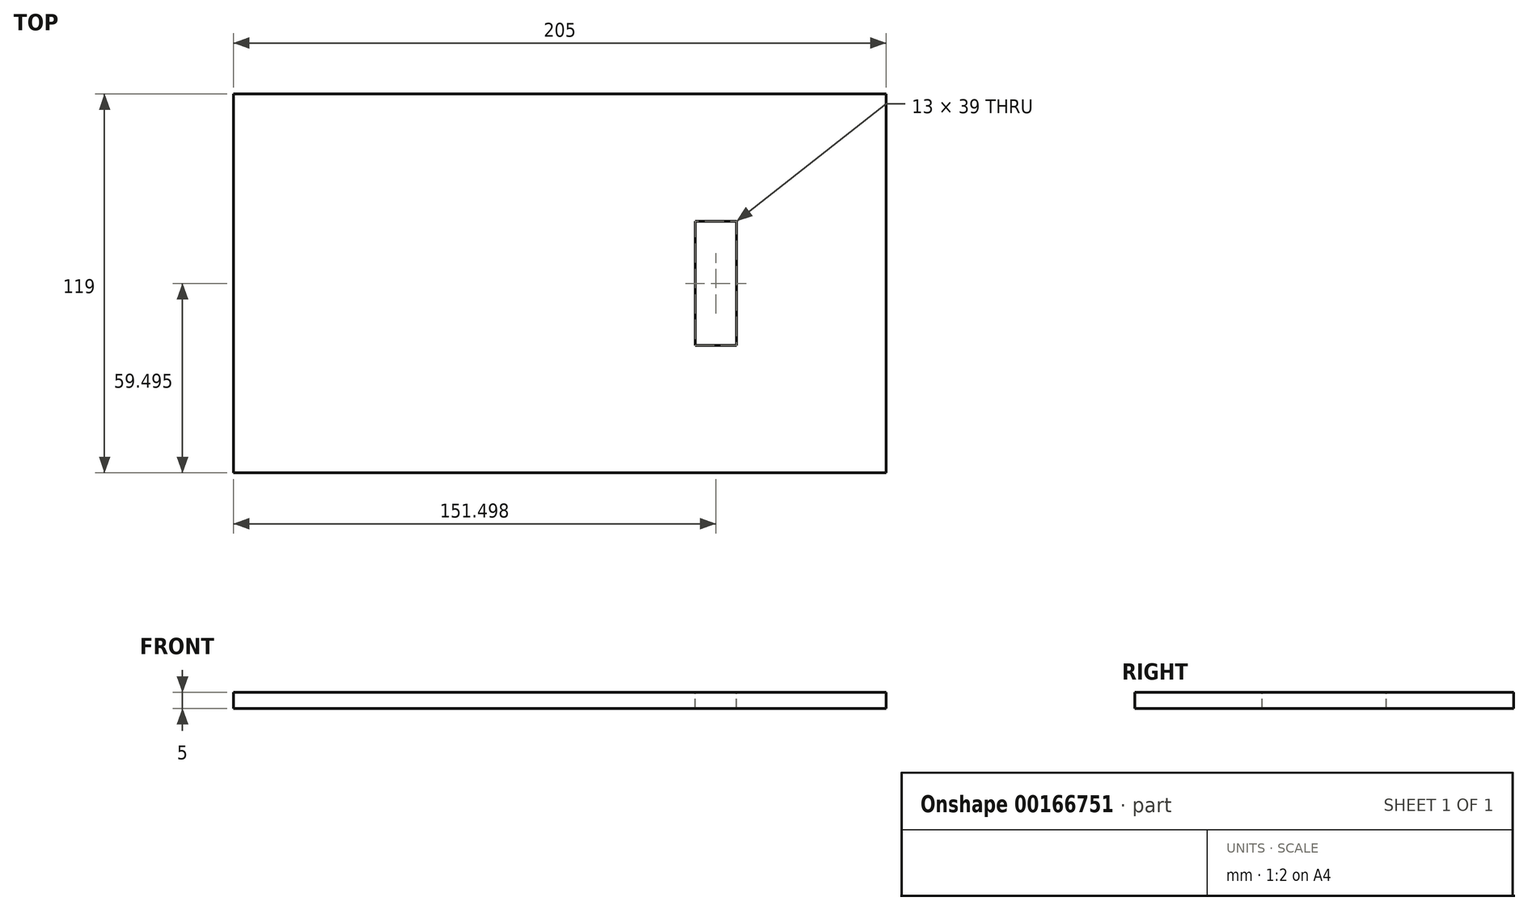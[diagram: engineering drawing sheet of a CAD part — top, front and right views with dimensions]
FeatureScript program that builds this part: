
annotation { "Feature Type Name" : "Feature", "Feature Type Description" : "" }
export const myFeature = defineFeature(function(context is Context, id is Id, definition is map)
    precondition{}
    {
        {
            var Q0;
            Q0=qCreatedBy(makeId("Top.planeOp"),FACE);
            var sketch = newSketch(context, id + "F0", { "sketchPlane" : qUnion([Q0])});
            skLineSegment(sketch, "E0.bottom", {"start": v(-194.6, 79.63) * mm, "end": v(10.4, 79.63) * mm});
            skLineSegment(sketch, "E0.top", {"start": v(-194.6, -39.37) * mm, "end": v(10.4, -39.37) * mm});
            skLineSegment(sketch, "E0.left", {"start": v(-194.6, 79.63) * mm, "end": v(-194.6, -39.37) * mm});
            skLineSegment(sketch, "E0.right", {"start": v(10.4, 79.63) * mm, "end": v(10.4, -39.37) * mm});
            skSolve(sketch);
        }
        {
            var Q0;
            Q0 = qSketchRegion(id + "F0", true);
            extrude(context, id + "F1", {"entities" : qUnion([Q0]), "depth" : 5 * mm, "offsetDistance" : 25 * mm});
        }
        {
            var Q0;
            Q0=makeQuery(id+"F1.opExtrude","CAP_FACE",FACE,{"disambiguationData":[OSD([sQuery(id+"F0.wireOp",EDGE,"E0.bottom"),sQuery(id+"F0.wireOp",EDGE,"E0.top"),sQuery(id+"F0.wireOp",EDGE,"E0.left"),sQuery(id+"F0.wireOp",EDGE,"E0.right")])],"isStart":false});
            var sketch = newSketch(context, id + "F2", { "sketchPlane" : qUnion([Q0])});
            skLineSegment(sketch, "E1.bottom", {"start": v(-49.6, 39.63) * mm, "end": v(-36.6, 39.63) * mm});
            skLineSegment(sketch, "E1.top", {"start": v(-49.6, 0.63) * mm, "end": v(-36.6, 0.63) * mm});
            skLineSegment(sketch, "E1.left", {"start": v(-49.6, 39.63) * mm, "end": v(-49.6, 0.63) * mm});
            skLineSegment(sketch, "E1.right", {"start": v(-36.6, 39.63) * mm, "end": v(-36.6, 0.63) * mm});
            skSolve(sketch);
        }
        {
            var Q0;
            Q0 = qSketchRegion(id + "F2", true);
            extrude(context, id + "F3", {"entities" : qUnion([Q0]), "operationType" : NewBodyOperationType.REMOVE, "oppositeDirection" : true, "depth" : 25 * mm, "offsetDistance" : 25 * mm});
        }
    });
